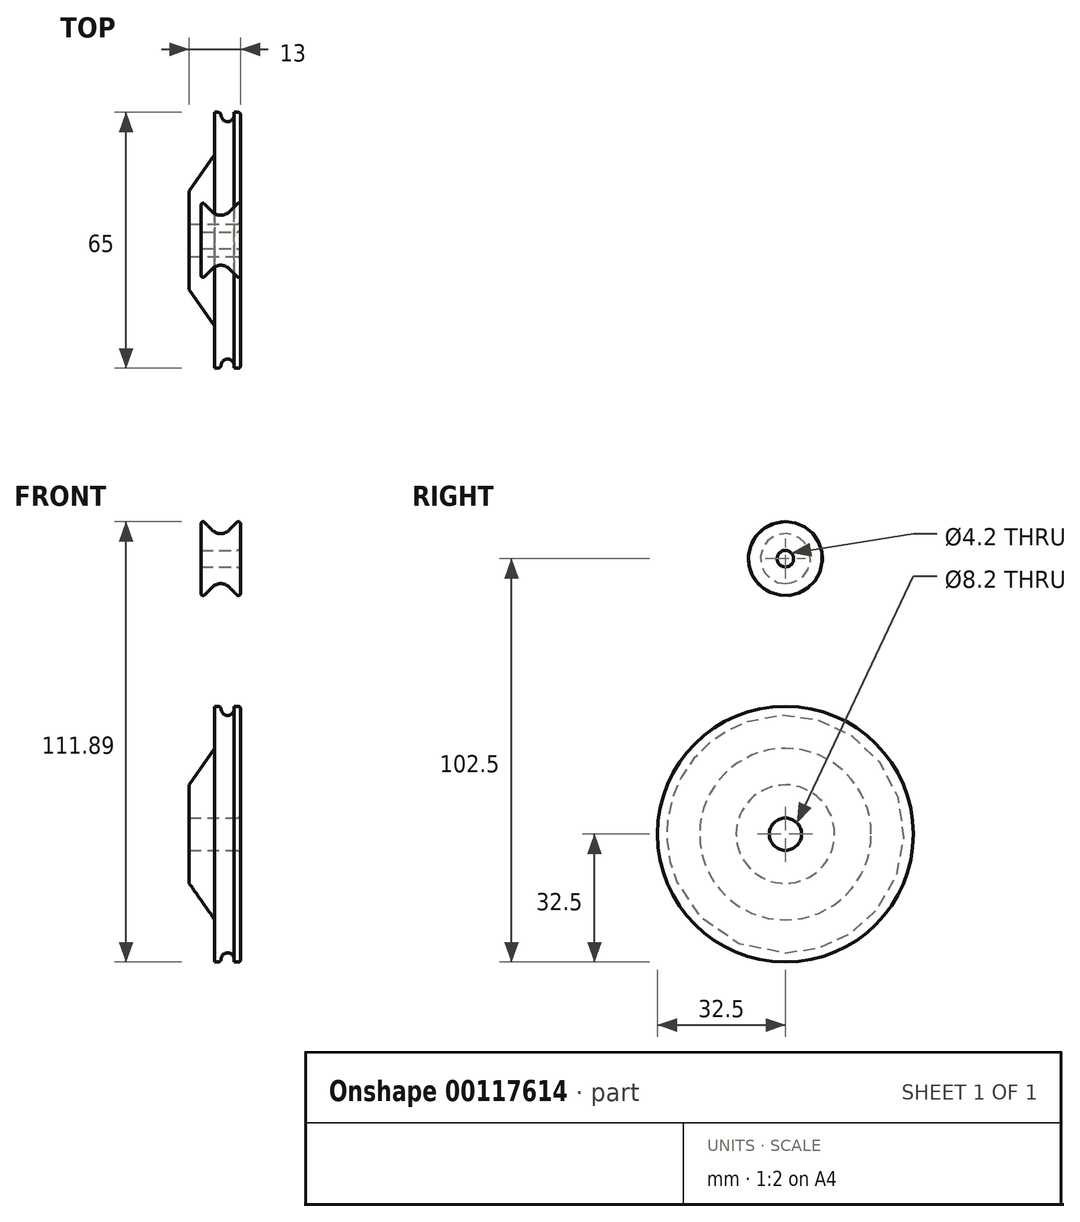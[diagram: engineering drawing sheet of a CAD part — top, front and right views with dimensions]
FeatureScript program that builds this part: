
annotation { "Feature Type Name" : "Feature", "Feature Type Description" : "" }
export const myFeature = defineFeature(function(context is Context, id is Id, definition is map)
    precondition{}
    {
        {
            var Q0;
            Q0=qCreatedBy(makeId("Front.planeOp"),FACE);
            var sketch = newSketch(context, id + "F0", { "sketchPlane" : qUnion([Q0])});
            skLineSegment(sketch, "E0", {"start": v(0, 4.1) * mm, "end": v(-13, 4.1) * mm});
            skLineSegment(sketch, "E1", {"start": v(-13, 4.1) * mm, "end": v(-13, 12.5) * mm});
            skLineSegment(sketch, "E2", {"start": v(-13, 12.5) * mm, "end": v(-6.5, 21.78) * mm});
            skLineSegment(sketch, "E3", {"start": v(-6.5, 21.78) * mm, "end": v(-6.5, 32.5) * mm});
            skLineSegment(sketch, "E4", {"start": v(-6.5, 32.5) * mm, "end": v(-4.9, 32.5) * mm});
            skLineSegment(sketch, "E5", {"start": v(-4.9, 32.5) * mm, "end": v(-4.9, 31.8) * mm});
            skArc(sketch, "E6", {"start": v(-4.9, 31.8) * mm, "mid": v(-3.25, 30.15) * mm, "end": v(-1.6, 31.8) * mm});
            skLineSegment(sketch, "E7", {"start": v(-1.6, 31.8) * mm, "end": v(-1.6, 32.5) * mm});
            skLineSegment(sketch, "E8", {"start": v(-1.6, 32.5) * mm, "end": v(0, 32.5) * mm});
            skLineSegment(sketch, "E9", {"start": v(0, 32.5) * mm, "end": v(0, 4.1) * mm});
            skCircle(sketch, "E10", {"center": v(-3.25, 31.8) * mm, "radius": 1.4 * mm, "construction": true});
            skLineSegment(sketch, "E11", {"start": v(0, 0) * mm, "end": v(-26.71, 0) * mm, "construction": true});
            skSolve(sketch);
        }
        {
            var Q0;
            Q0 = qSketchRegion(id + "F0", true);
            var Q1;
            Q1=sQuery(id+"F0.wireOp",EDGE,"E11");
            revolve(context, id + "F1", {"entities" : qUnion([Q0]), "axis" : qUnion([Q1]), "revolveType" : RevolveType.FULL});
        }
        {
            var Q0;
            Q0=makeQuery(id+"F1.opRevolve","SWEPT_EDGE",EDGE,{"disambiguationData":[OSD([sQuery(id+"F0.wireOp",EDGE,"E0"),sQuery(id+"F0.wireOp",EDGE,"E9")])]});
            fillet(context, id + "F2", {"entities" : qUnion([Q0]), "radius" : 1 * mm, "tangentPropagation" : true, "allowEdgeOverflow" : false});
        }
        {
            var Q0;
            Q0=makeQuery(id+"F1.opRevolve","SWEPT_EDGE",EDGE,{"disambiguationData":[OSD([sQuery(id+"F0.wireOp",EDGE,"E8"),sQuery(id+"F0.wireOp",EDGE,"E9")])]});
            fillet(context, id + "F3", {"entities" : qUnion([Q0]), "radius" : 0.5 * mm, "tangentPropagation" : true, "allowEdgeOverflow" : false});
        }
        {
            var Q0;
            Q0=makeQuery(id+"F1.opRevolve","SWEPT_EDGE",EDGE,{"disambiguationData":[OSD([sQuery(id+"F0.wireOp",EDGE,"E4"),sQuery(id+"F0.wireOp",EDGE,"E5")])]});
            fillet(context, id + "F4", {"entities" : qUnion([Q0]), "radius" : 0.8 * mm, "tangentPropagation" : true, "allowEdgeOverflow" : false});
        }
        {
            var Q0;
            Q0=qCreatedBy(makeId("Front.planeOp"),FACE);
            var sketch = newSketch(context, id + "F5", { "sketchPlane" : qUnion([Q0])});
            skLineSegment(sketch, "E12", {"start": v(0, 70) * mm, "end": v(-50.25, 70) * mm, "construction": true});
            skLineSegment(sketch, "E13", {"start": v(0, 72.1) * mm, "end": v(-10, 72.1) * mm});
            skLineSegment(sketch, "E14", {"start": v(-10, 72.1) * mm, "end": v(-10, 80.1) * mm});
            skLineSegment(sketch, "E15", {"start": v(-10, 80.1) * mm, "end": v(-5, 75.1) * mm});
            skLineSegment(sketch, "E16", {"start": v(-5, 75.1) * mm, "end": v(0, 80.1) * mm});
            skLineSegment(sketch, "E17", {"start": v(0, 80.1) * mm, "end": v(0, 72.1) * mm});
            skLineSegment(sketch, "E18", {"start": v(-5, 70) * mm, "end": v(-5, 77.28) * mm, "construction": true});
            skPoint(sketch, "E18.startSnap0", {"position": v(-5, 72.1) * mm});
            skCircle(sketch, "E19", {"center": v(-5, 77.9) * mm, "radius": 1.4 * mm, "construction": true});
            skSolve(sketch);
        }
        {
            var Q0;
            Q0 = qSketchRegion(id + "F5", true);
            var Q1;
            Q1=sQuery(id+"F5.wireOp",EDGE,"E12");
            revolve(context, id + "F6", {"entities" : qUnion([Q0]), "axis" : qUnion([Q1]), "revolveType" : RevolveType.FULL});
        }
        {
            var Q0;
            Q0=makeQuery(id+"F6.opRevolve","SWEPT_EDGE",EDGE,{"disambiguationData":[OSD([sQuery(id+"F5.wireOp",EDGE,"E15"),sQuery(id+"F5.wireOp",EDGE,"E16")])]});
            fillet(context, id + "F7", {"entities" : qUnion([Q0]), "radius" : 3 * mm, "tangentPropagation" : true, "allowEdgeOverflow" : false});
        }
        {
            var Q0;
            Q0=makeQuery(id+"F6.opRevolve","SWEPT_EDGE",EDGE,{"disambiguationData":[OSD([sQuery(id+"F5.wireOp",EDGE,"E16"),sQuery(id+"F5.wireOp",EDGE,"E17")])]});
            var Q1;
            Q1=makeQuery(id+"F6.opRevolve","SWEPT_EDGE",EDGE,{"disambiguationData":[OSD([sQuery(id+"F5.wireOp",EDGE,"E14"),sQuery(id+"F5.wireOp",EDGE,"E15")])]});
            fillet(context, id + "F8", {"entities" : qUnion([Q0, Q1]), "radius" : 0.5 * mm, "tangentPropagation" : true, "allowEdgeOverflow" : false});
        }
        {
            var Q0;
            Q0=makeQuery(id+"F6.opRevolve","SWEPT_EDGE",EDGE,{"disambiguationData":[OSD([sQuery(id+"F5.wireOp",EDGE,"E13"),sQuery(id+"F5.wireOp",EDGE,"E17")])]});
            fillet(context, id + "F9", {"entities" : qUnion([Q0]), "radius" : 1 * mm, "tangentPropagation" : true, "allowEdgeOverflow" : false});
        }
    });
